# Revit family: steckdose.pdf
name_source: partatom
category: Generic Models
revit_build: Autodesk Revit 2017 (Build: 20160225_1515(x64)
units: mm (PartAtom-declared; Revit-internal decimal feet)

## family parameters
Always vertical = Yes
Can host rebar = No
Cut with Voids When Loaded = No
Part Type = Normal
Room Calculation Point = No
Round Connector Dimension = Use Diameter
Shared = No
Work Plane-Based = No

## types (6) — shared parameters
Height = 40 mm  [stored 0.131234 ft]
Manufacturer = OBO BETTERMANN
Material = Polycarbonat
URL = http://www.obo-bettermann.com
Width = 45 mm  [stored 0.147638 ft]

## per-type parameters (varying)
| type | GTIN | Manufacturer Art.No. |
| STD-D3C RW2 | 4012196050550 | 6120482 |
| STD-D3C ROR2 | 4012196050567 | 6120484 |
| STD-D3C MZGN2 | 4012196050581 | 6120486 |
| STD-D3C SRO2 | 4012196050611 | 6120488 |
| STD-D3C SWGR2 | 4012196050628 | 6120490 |
| STD-D3C AL2 | 4012196050635 | 6120492 |

note: column(s) folded — value = type name in every type: Article Type

note: [stored X ft] marks values corroborated as IEEE doubles in the binary element streams (Revit-internal decimal feet)

## geometry (parser evidence)
native form markers: Sweep x2
no freeform markers — native parametric forms only
